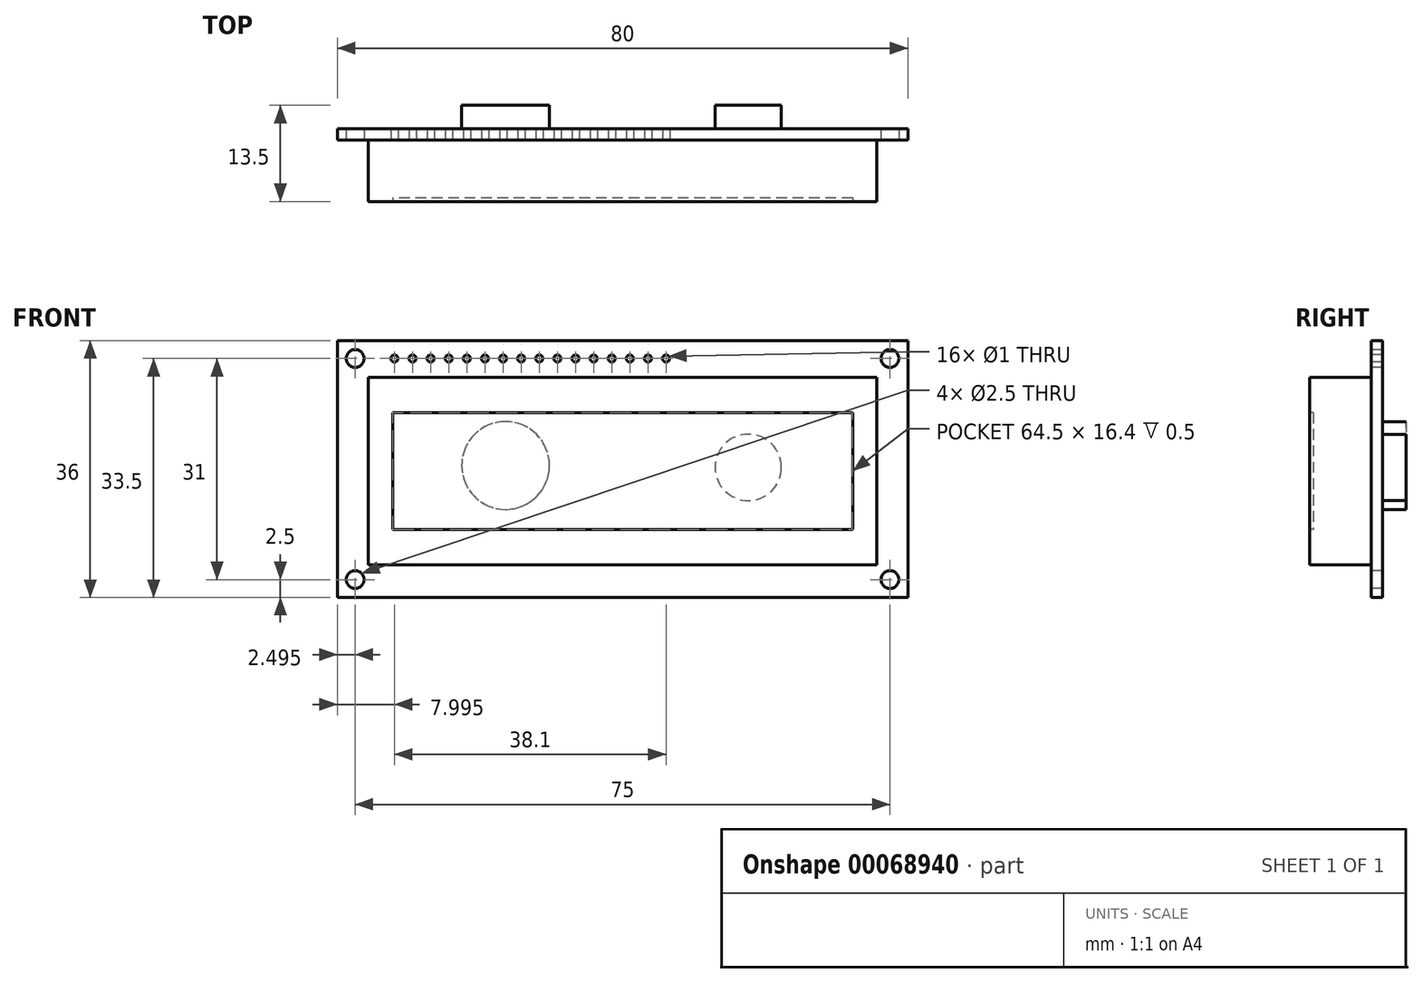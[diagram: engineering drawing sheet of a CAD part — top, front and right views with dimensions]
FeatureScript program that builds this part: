
annotation { "Feature Type Name" : "Feature", "Feature Type Description" : "" }
export const myFeature = defineFeature(function(context is Context, id is Id, definition is map)
    precondition{}
    {
        {
            var Q0;
            Q0=qCreatedBy(makeId("Front.planeOp"),FACE);
            var sketch = newSketch(context, id + "F0", { "sketchPlane" : qUnion([Q0])});
            skLineSegment(sketch, "E0.bottom", {"start": v(-4.1, -4.25) * mm, "end": v(75.9, -4.25) * mm});
            skLineSegment(sketch, "E0.top", {"start": v(-4.1, 31.75) * mm, "end": v(75.9, 31.75) * mm});
            skLineSegment(sketch, "E0.left", {"start": v(-4.1, -4.25) * mm, "end": v(-4.1, 31.75) * mm});
            skLineSegment(sketch, "E0.right", {"start": v(75.9, -4.25) * mm, "end": v(75.9, 31.75) * mm});
            skSolve(sketch);
        }
        {
            var Q0;
            Q0 = qSketchRegion(id + "F0", true);
            extrude(context, id + "F1", {"entities" : qUnion([Q0]), "depth" : 1.6 * mm});
        }
        {
            var Q0;
            Q0=makeQuery(id+"F1.opExtrude","CAP_FACE",FACE,{"disambiguationData":[OSD([sQuery(id+"F0.wireOp",EDGE,"E0.bottom"),sQuery(id+"F0.wireOp",EDGE,"E0.top"),sQuery(id+"F0.wireOp",EDGE,"E0.left"),sQuery(id+"F0.wireOp",EDGE,"E0.right")])],"isStart":false});
            var sketch = newSketch(context, id + "F2", { "sketchPlane" : qUnion([Q0])});
            skLineSegment(sketch, "E1.bottom", {"start": v(0.26, 0.3) * mm, "end": v(71.56, 0.3) * mm});
            skLineSegment(sketch, "E1.top", {"start": v(0.26, 26.6) * mm, "end": v(71.56, 26.6) * mm});
            skLineSegment(sketch, "E1.left", {"start": v(0.26, 0.3) * mm, "end": v(0.26, 26.6) * mm});
            skLineSegment(sketch, "E1.right", {"start": v(71.56, 0.3) * mm, "end": v(71.56, 26.6) * mm});
            skLineSegment(sketch, "E2", {"start": v(35.9, 0.3) * mm, "end": v(35.9, 31.75) * mm, "construction": true});
            skSolve(sketch);
        }
        {
            var Q0;
            Q0 = qSketchRegion(id + "F2", true);
            extrude(context, id + "F3", {"entities" : qUnion([Q0]), "operationType" : NewBodyOperationType.ADD, "depth" : 8.6 * mm});
        }
        {
            var Q0;
            Q0=makeQuery(id+"F3.opExtrude","CAP_FACE",FACE,{"disambiguationData":[OSD([sQuery(id+"F2.wireOp",EDGE,"E1.bottom"),sQuery(id+"F2.wireOp",EDGE,"E1.top"),sQuery(id+"F2.wireOp",EDGE,"E1.left"),sQuery(id+"F2.wireOp",EDGE,"E1.right")])],"isStart":false});
            var sketch = newSketch(context, id + "F4", { "sketchPlane" : qUnion([Q0])});
            skLineSegment(sketch, "E3.bottom", {"start": v(68.16, 21.65) * mm, "end": v(3.66, 21.65) * mm});
            skLineSegment(sketch, "E3.top", {"start": v(68.16, 5.25) * mm, "end": v(3.66, 5.25) * mm});
            skLineSegment(sketch, "E3.left", {"start": v(68.16, 21.65) * mm, "end": v(68.16, 5.25) * mm});
            skLineSegment(sketch, "E3.right", {"start": v(3.66, 21.65) * mm, "end": v(3.66, 5.25) * mm});
            skPoint(sketch, "E3.middle", {"position": v(35.9, 13.45) * mm});
            skPoint(sketch, "E3.middle.positionSnap0", {"position": v(71.56, 13.45) * mm});
            skPoint(sketch, "E3.middle.positionSnap1", {"position": v(35.9, 26.6) * mm});
            skPoint(sketch, "E3.centerSnap0", {"position": v(71.56, 13.45) * mm});
            skPoint(sketch, "E3.centerSnap1", {"position": v(35.9, 26.6) * mm});
            skSolve(sketch);
        }
        {
            var Q0;
            Q0 = qSketchRegion(id + "F4", true);
            extrude(context, id + "F5", {"entities" : qUnion([Q0]), "operationType" : NewBodyOperationType.REMOVE, "oppositeDirection" : true, "depth" : 0.5 * mm});
        }
        {
            var Q0;
            Q0=makeQuery(id+"F1.opExtrude","CAP_FACE",FACE,{"disambiguationData":[OSD([sQuery(id+"F0.wireOp",EDGE,"E0.bottom"),sQuery(id+"F0.wireOp",EDGE,"E0.top"),sQuery(id+"F0.wireOp",EDGE,"E0.left"),sQuery(id+"F0.wireOp",EDGE,"E0.right")])],"isStart":false});
            var sketch = newSketch(context, id + "F6", { "sketchPlane" : qUnion([Q0])});
            skLineSegment(sketch, "E4.0", {"start": v(-4.1, 31.75) * mm, "end": v(75.9, 31.75) * mm, "construction": true});
            skLineSegment(sketch, "E5.0", {"start": v(-4.1, -4.25) * mm, "end": v(-4.1, 31.75) * mm, "construction": true});
            skLineSegment(sketch, "E6.0", {"start": v(-4.1, -4.25) * mm, "end": v(75.9, -4.25) * mm, "construction": true});
            skLineSegment(sketch, "E7.0", {"start": v(75.9, -4.25) * mm, "end": v(75.9, 31.75) * mm, "construction": true});
            skCircle(sketch, "E8", {"center": v(-1.6, 29.25) * mm, "radius": 1.25 * mm});
            skCircle(sketch, "E9", {"center": v(73.4, 29.25) * mm, "radius": 1.25 * mm});
            skCircle(sketch, "E10", {"center": v(73.4, -1.75) * mm, "radius": 1.25 * mm});
            skCircle(sketch, "E11", {"center": v(-1.6, -1.75) * mm, "radius": 1.25 * mm});
            skLineSegment(sketch, "E12.bottom", {"start": v(73.4, 29.25) * mm, "end": v(-1.6, 29.25) * mm, "construction": true});
            skLineSegment(sketch, "E12.top", {"start": v(73.4, -1.75) * mm, "end": v(-1.6, -1.75) * mm, "construction": true});
            skLineSegment(sketch, "E12.left", {"start": v(73.4, 29.25) * mm, "end": v(73.4, -1.75) * mm, "construction": true});
            skLineSegment(sketch, "E12.right", {"start": v(-1.6, 29.25) * mm, "end": v(-1.6, -1.75) * mm, "construction": true});
            skPoint(sketch, "E12.middle", {"position": v(35.9, 13.75) * mm});
            skPoint(sketch, "E12.middle.positionSnap0", {"position": v(75.9, 13.75) * mm});
            skPoint(sketch, "E12.middle.positionSnap1", {"position": v(35.9, 26.6) * mm});
            skPoint(sketch, "E12.centerSnap0", {"position": v(75.9, 13.75) * mm});
            skPoint(sketch, "E12.centerSnap1", {"position": v(35.9, 26.6) * mm});
            skSolve(sketch);
        }
        {
            var Q0;
            Q0 = qSketchRegion(id + "F6", true);
            extrude(context, id + "F7", {"entities" : qUnion([Q0]), "operationType" : NewBodyOperationType.REMOVE, "endBound" : BoundingType.THROUGH_ALL, "oppositeDirection" : true, "depth" : 25 * mm});
        }
        {
            var Q0;
            Q0=makeQuery(id+"F1.opExtrude","CAP_FACE",FACE,{"disambiguationData":[OSD([sQuery(id+"F0.wireOp",EDGE,"E0.bottom"),sQuery(id+"F0.wireOp",EDGE,"E0.top"),sQuery(id+"F0.wireOp",EDGE,"E0.left"),sQuery(id+"F0.wireOp",EDGE,"E0.right")])],"isStart":false});
            var sketch = newSketch(context, id + "F8", { "sketchPlane" : qUnion([Q0])});
            skCircle(sketch, "E13", {"center": v(3.9, 29.25) * mm, "radius": 0.5 * mm});
            skCircle(sketch, "E14.1.0.0", {"center": v(6.45, 29.25) * mm, "radius": 0.5 * mm});
            skCircle(sketch, "E14.2.0.0", {"center": v(8.99, 29.25) * mm, "radius": 0.5 * mm});
            skCircle(sketch, "E14.3.0.0", {"center": v(11.53, 29.25) * mm, "radius": 0.5 * mm});
            skCircle(sketch, "E14.4.0.0", {"center": v(14.07, 29.25) * mm, "radius": 0.5 * mm});
            skCircle(sketch, "E14.5.0.0", {"center": v(16.6, 29.25) * mm, "radius": 0.5 * mm});
            skCircle(sketch, "E14.6.0.0", {"center": v(19.15, 29.25) * mm, "radius": 0.5 * mm});
            skCircle(sketch, "E14.7.0.0", {"center": v(21.69, 29.25) * mm, "radius": 0.5 * mm});
            skCircle(sketch, "E14.8.0.0", {"center": v(24.23, 29.25) * mm, "radius": 0.5 * mm});
            skCircle(sketch, "E14.9.0.0", {"center": v(26.77, 29.25) * mm, "radius": 0.5 * mm});
            skCircle(sketch, "E14.10.0.0", {"center": v(29.3, 29.25) * mm, "radius": 0.5 * mm});
            skCircle(sketch, "E14.11.0.0", {"center": v(31.85, 29.25) * mm, "radius": 0.5 * mm});
            skCircle(sketch, "E14.12.0.0", {"center": v(34.39, 29.25) * mm, "radius": 0.5 * mm});
            skCircle(sketch, "E14.13.0.0", {"center": v(36.93, 29.25) * mm, "radius": 0.5 * mm});
            skCircle(sketch, "E14.14.0.0", {"center": v(39.47, 29.25) * mm, "radius": 0.5 * mm});
            skCircle(sketch, "E14.15.0.0", {"center": v(42, 29.25) * mm, "radius": 0.5 * mm});
            skLineSegment(sketch, "E14.direction1", {"start": v(3.9, 29.25) * mm, "end": v(6.45, 29.25) * mm, "construction": true});
            skSolve(sketch);
        }
        {
            var Q0;
            Q0 = qSketchRegion(id + "F8", true);
            extrude(context, id + "F9", {"entities" : qUnion([Q0]), "operationType" : NewBodyOperationType.REMOVE, "endBound" : BoundingType.THROUGH_ALL, "oppositeDirection" : true, "depth" : 25 * mm});
        }
        {
            var Q0;
            Q0=makeQuery(id+"F1.opExtrude","CAP_FACE",FACE,{"disambiguationData":[OSD([sQuery(id+"F0.wireOp",EDGE,"E0.bottom"),sQuery(id+"F0.wireOp",EDGE,"E0.top"),sQuery(id+"F0.wireOp",EDGE,"E0.left"),sQuery(id+"F0.wireOp",EDGE,"E0.right")])],"isStart":true});
            var sketch = newSketch(context, id + "F10", { "sketchPlane" : qUnion([Q0])});
            skCircle(sketch, "E15", {"center": v(-53.53, 13.98) * mm, "radius": 4.65 * mm});
            skCircle(sketch, "E16", {"center": v(-19.5, 14.24) * mm, "radius": 6.16 * mm});
            skSolve(sketch);
        }
        {
            var Q0;
            Q0 = qSketchRegion(id + "F10", true);
            extrude(context, id + "F11", {"entities" : qUnion([Q0]), "operationType" : NewBodyOperationType.ADD, "depth" : 3.3 * mm});
        }
    });
